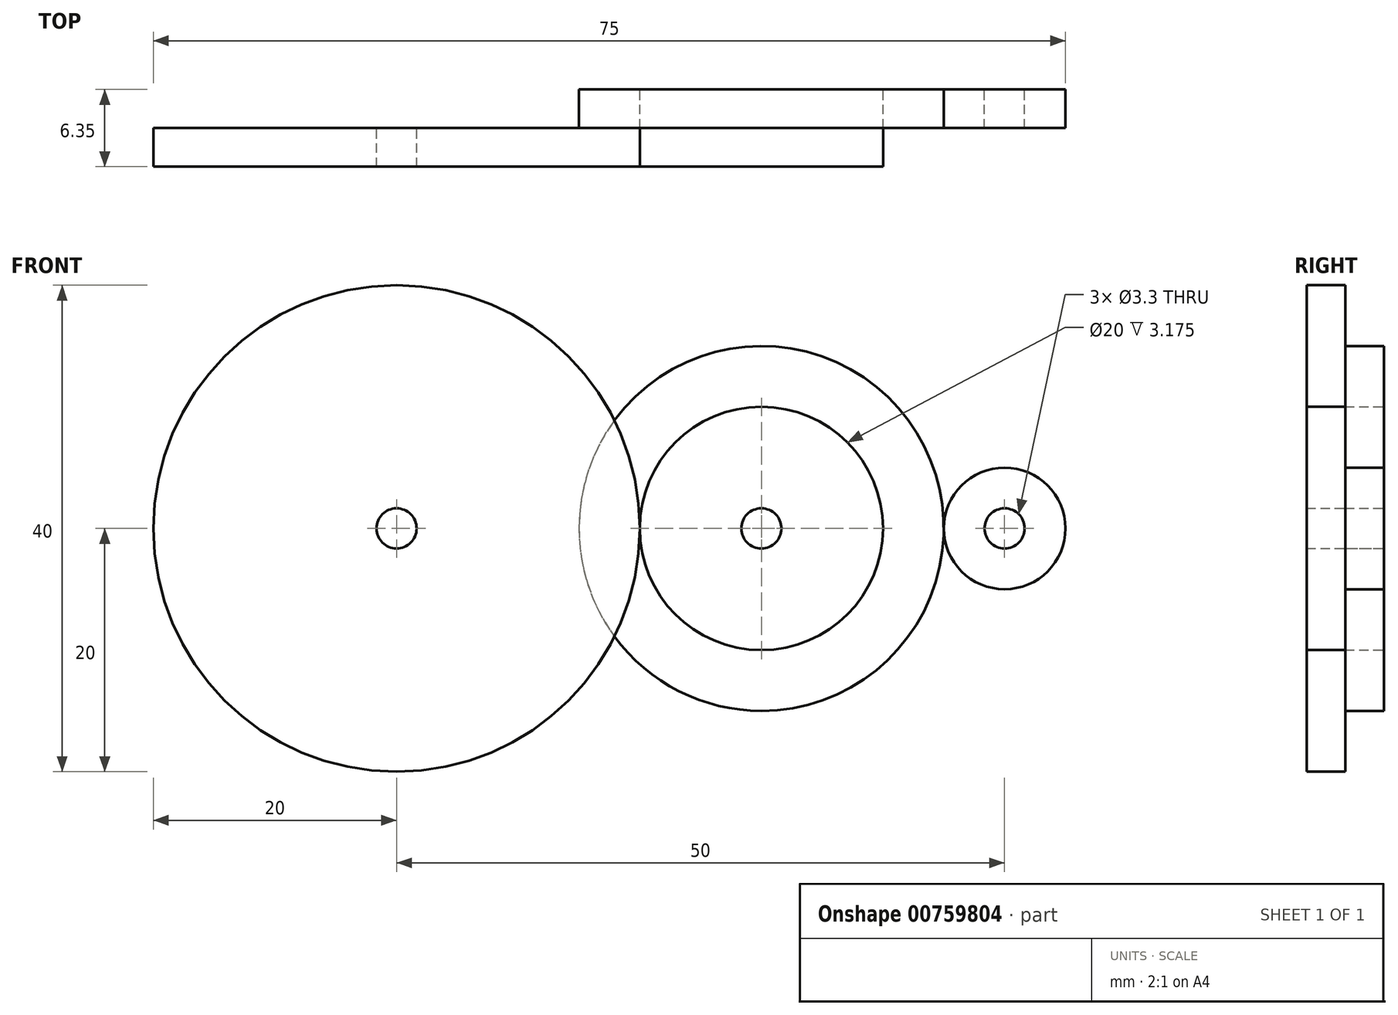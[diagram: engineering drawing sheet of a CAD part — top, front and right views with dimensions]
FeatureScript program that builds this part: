
annotation { "Feature Type Name" : "Feature", "Feature Type Description" : "" }
export const myFeature = defineFeature(function(context is Context, id is Id, definition is map)
    precondition{}
    {
        {
            var Q0;
            Q0=qCreatedBy(makeId("Front.planeOp"),FACE);
            var sketch = newSketch(context, id + "F0", { "sketchPlane" : qUnion([Q0])});
            skCircle(sketch, "E0", {"center": v(0, 0) * mm, "radius": 5 * mm});
            skCircle(sketch, "E1", {"center": v(-20, 0) * mm, "radius": 15 * mm});
            skCircle(sketch, "E2", {"center": v(-20, 0) * mm, "radius": 10 * mm});
            skCircle(sketch, "E3", {"center": v(0, 0) * mm, "radius": 1.65 * mm});
            skCircle(sketch, "E4", {"center": v(-20, 0) * mm, "radius": 1.65 * mm});
            skCircle(sketch, "E5", {"center": v(20, 0) * mm, "radius": 1.65 * mm});
            skSolve(sketch);
        }
        {
            var Q0;
            Q0=makeQuery(id+"F0.imprint","IMPRINT",FACE,{"disambiguationData":[TD([[makeQuery(id+"F0.imprint","IMPRINT",EDGE,{"derivedFrom":sQuery(id+"F0.wireOp",EDGE,"E0")}),1.0]])]});
            extrude(context, id + "F1", {"entities" : qUnion([Q0]), "depth" : 3.17 * mm, "offsetDistance" : 25.4 * mm});
        }
        {
            var Q0;
            Q0=makeQuery(id+"F0.imprint","IMPRINT",FACE,{"disambiguationData":[TD([[makeQuery(id+"F0.imprint","IMPRINT",EDGE,{"derivedFrom":sQuery(id+"F0.wireOp",EDGE,"E2")}),-1.0]])]});
            extrude(context, id + "F2", {"entities" : qUnion([Q0]), "depth" : 3.17 * mm, "offsetDistance" : 25.4 * mm});
        }
        {
            var Q0;
            Q0=makeQuery(id+"F0.imprint","IMPRINT",FACE,{"disambiguationData":[TD([[makeQuery(id+"F0.imprint","IMPRINT",EDGE,{"derivedFrom":sQuery(id+"F0.wireOp",EDGE,"E2")}),1.0]])]});
            extrude(context, id + "F3", {"entities" : qUnion([Q0]), "depth" : 6.35 * mm, "offsetDistance" : 25.4 * mm});
        }
        {
            var Q0;
            Q0=makeQuery(id+"F2.opExtrude","CAP_FACE",FACE,{"disambiguationData":[OSD([sQuery(id+"F0.wireOp",EDGE,"E1"),sQuery(id+"F0.wireOp",EDGE,"E2")])],"isStart":false});
            var sketch = newSketch(context, id + "F4", { "sketchPlane" : qUnion([Q0])});
            skCircle(sketch, "E6", {"center": v(-50, 0) * mm, "radius": 20 * mm});
            skCircle(sketch, "E7", {"center": v(-50, 0) * mm, "radius": 1.65 * mm});
            skSolve(sketch);
        }
        {
            var Q0;
            Q0=qSketchRegion(id+"F4",true);
            extrude(context, id + "F5", {"entities" : qUnion([Q0]), "depth" : 3.17 * mm, "offsetDistance" : 25.4 * mm});
        }
    });
